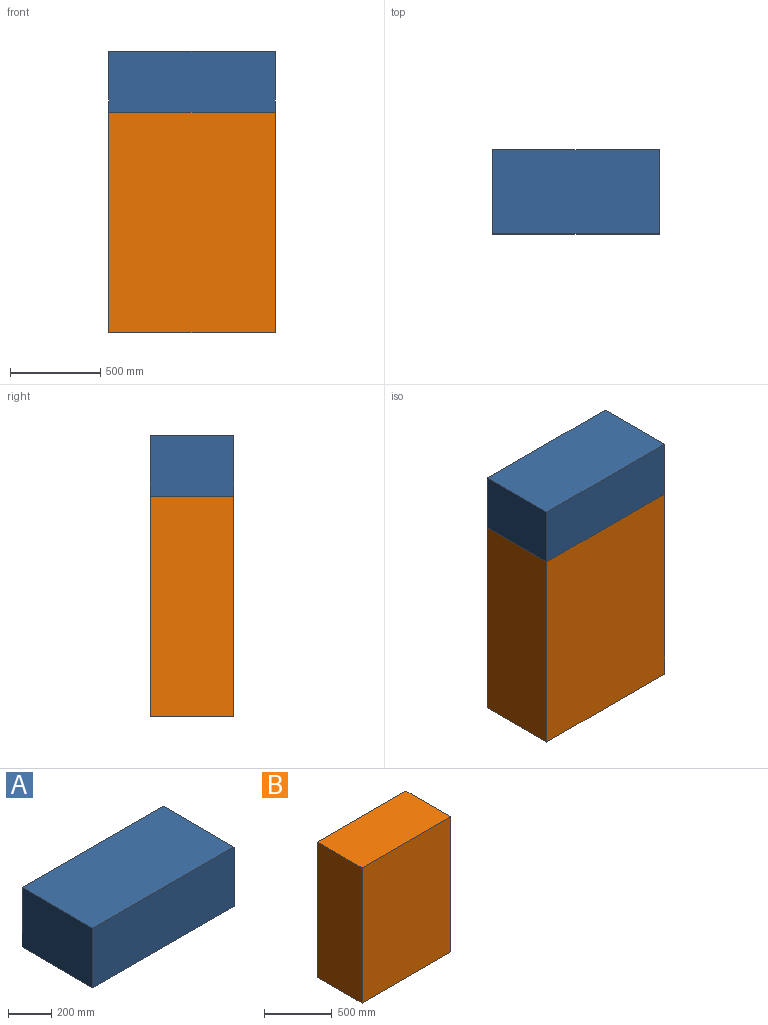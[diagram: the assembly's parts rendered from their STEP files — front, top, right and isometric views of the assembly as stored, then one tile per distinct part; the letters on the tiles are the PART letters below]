
ASSEMBLY  parts=2 mates=1
PART A: 6 faces, bbox 920.8x463.6x336.6 mm
  f0: plane 920.75x336.55mm, normal (0,1,0), area 309878.4mm2, adj f1,f3,f4,f5
  f1: plane 463.55x336.55mm, normal (-1,0,0), area 156007.8mm2, adj f0,f2,f4,f5
  f2: plane 920.75x336.55mm, normal (0,-1,0), area 309878.4mm2, adj f1,f3,f4,f5
  f3: plane 463.55x336.55mm, normal (1,0,0), area 156007.8mm2, adj f0,f2,f4,f5
  f4: plane 920.75x463.55mm, normal (0,0,1), area 426813.7mm2, adj f0,f1,f2,f3
  f5: plane 920.75x463.55mm, normal (0,0,-1), area 426813.7mm2, adj f0,f1,f2,f3
PART B: 6 faces, bbox 920.8x463.6x1219.2 mm
  f0: plane 1219.2x920.75mm, normal (0,1,0), area 1122578.4mm2, adj f1,f3,f4,f5
  f1: plane 1219.2x463.55mm, normal (-1,0,0), area 565160.2mm2, adj f0,f2,f4,f5
  f2: plane 1219.2x920.75mm, normal (0,-1,0), area 1122578.4mm2, adj f1,f3,f4,f5
  f3: plane 1219.2x463.55mm, normal (1,0,0), area 565160.2mm2, adj f0,f2,f4,f5
  f4: plane 920.75x463.55mm, normal (0,0,1), area 426813.7mm2, adj f0,f1,f2,f3
  f5: plane 920.75x463.55mm, normal (0,0,-1), area 426813.7mm2, adj f0,f1,f2,f3
PLACE A t=(0,0,1219.2)mm
PLACE B at identity
MATE fastened B.f4 <-> A.f5  axis (0,0,1) through (0,0,1219.2)mm
